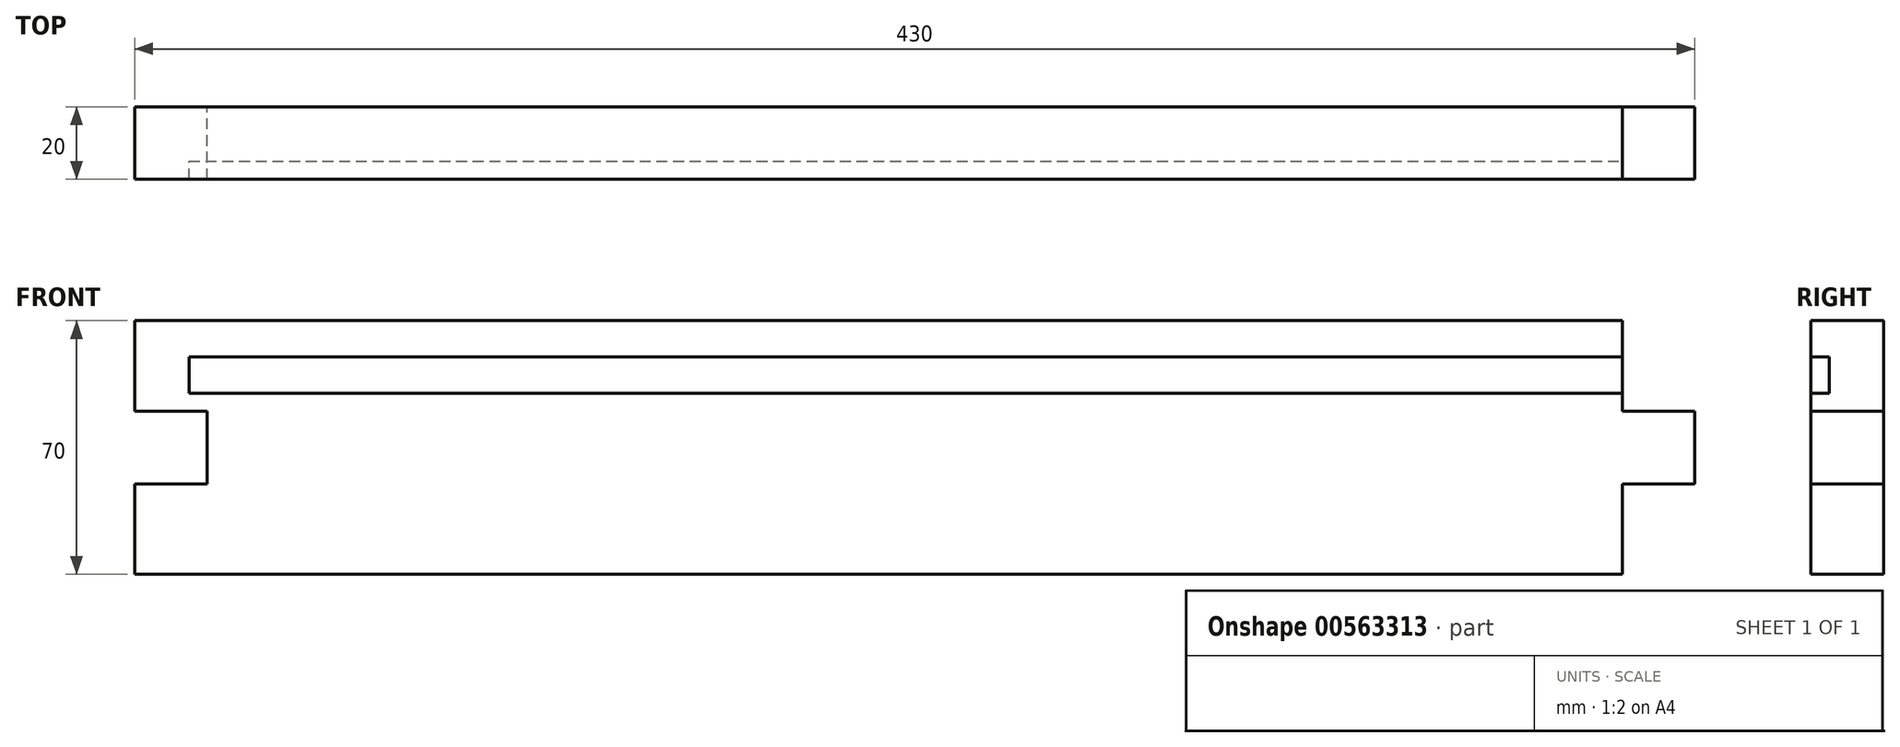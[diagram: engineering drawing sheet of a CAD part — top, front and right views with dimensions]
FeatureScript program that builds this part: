
annotation { "Feature Type Name" : "Feature", "Feature Type Description" : "" }
export const myFeature = defineFeature(function(context is Context, id is Id, definition is map)
    precondition{}
    {
        {
            var Q0;
            Q0=qCreatedBy(makeId("Top.planeOp"),FACE);
            var sketch = newSketch(context, id + "F0", { "sketchPlane" : qUnion([Q0])});
            skLineSegment(sketch, "E0.bottom", {"start": v(-404.74, -7.95) * mm, "end": v(25.26, -7.95) * mm});
            skLineSegment(sketch, "E0.top", {"start": v(-404.74, -27.95) * mm, "end": v(25.26, -27.95) * mm});
            skLineSegment(sketch, "E0.left", {"start": v(-404.74, -7.95) * mm, "end": v(-404.74, -27.95) * mm});
            skLineSegment(sketch, "E0.right", {"start": v(25.26, -7.95) * mm, "end": v(25.26, -27.95) * mm});
            skSolve(sketch);
        }
        {
            var Q0;
            Q0=qSketchRegion(id+"F0",true);
            extrude(context, id + "F1", {"entities" : qUnion([Q0]), "depth" : 70 * mm, "offsetDistance" : 25 * mm});
        }
        {
            var Q0;
            Q0=makeQuery(id+"F1.opExtrude","SWEPT_FACE",FACE,{"disambiguationData":[OSD([sQuery(id+"F0.wireOp",EDGE,"E0.right")])]});
            var sketch = newSketch(context, id + "F2", { "sketchPlane" : qUnion([Q0])});
            skLineSegment(sketch, "E1.bottom", {"start": v(-27.95, 60) * mm, "end": v(-22.95, 60) * mm});
            skLineSegment(sketch, "E1.top", {"start": v(-27.95, 50) * mm, "end": v(-22.95, 50) * mm});
            skLineSegment(sketch, "E1.left", {"start": v(-27.95, 60) * mm, "end": v(-27.95, 50) * mm});
            skLineSegment(sketch, "E1.right", {"start": v(-22.95, 60) * mm, "end": v(-22.95, 50) * mm});
            skSolve(sketch);
        }
        {
            var Q0;
            Q0=qSketchRegion(id+"F2",true);
            extrude(context, id + "F3", {"entities" : qUnion([Q0]), "operationType" : NewBodyOperationType.REMOVE, "oppositeDirection" : true, "depth" : 415 * mm, "offsetDistance" : 25 * mm, "hasSecondDirection" : true, "secondDirectionOppositeDirection" : true, "secondDirectionDepth" : 15 * mm});
        }
        {
            var Q0;
            Q0=makeQuery(id+"F1.opExtrude","SWEPT_FACE",FACE,{"disambiguationData":[OSD([sQuery(id+"F0.wireOp",EDGE,"E0.bottom")])]});
            var sketch = newSketch(context, id + "F4", { "sketchPlane" : qUnion([Q0])});
            skLineSegment(sketch, "E2.bottom", {"start": v(-25.26, 70) * mm, "end": v(-5.26, 70) * mm});
            skLineSegment(sketch, "E2.top", {"start": v(-25.26, 45) * mm, "end": v(-5.26, 45) * mm});
            skLineSegment(sketch, "E2.left", {"start": v(-25.26, 70) * mm, "end": v(-25.26, 45) * mm});
            skLineSegment(sketch, "E2.right", {"start": v(-5.26, 70) * mm, "end": v(-5.26, 45) * mm});
            skLineSegment(sketch, "E3.bottom", {"start": v(-25.26, 0) * mm, "end": v(-5.26, 0) * mm});
            skLineSegment(sketch, "E3.top", {"start": v(-25.26, 25) * mm, "end": v(-5.26, 25) * mm});
            skLineSegment(sketch, "E3.left", {"start": v(-25.26, 0) * mm, "end": v(-25.26, 25) * mm});
            skLineSegment(sketch, "E3.right", {"start": v(-5.26, 0) * mm, "end": v(-5.26, 25) * mm});
            skLineSegment(sketch, "E4.bottom", {"start": v(404.74, 45) * mm, "end": v(384.74, 45) * mm});
            skLineSegment(sketch, "E4.top", {"start": v(404.74, 25) * mm, "end": v(384.74, 25) * mm});
            skLineSegment(sketch, "E4.left", {"start": v(404.74, 45) * mm, "end": v(404.74, 25) * mm});
            skLineSegment(sketch, "E4.right", {"start": v(384.74, 45) * mm, "end": v(384.74, 25) * mm});
            skSolve(sketch);
        }
        {
            var Q0;
            Q0=makeQuery(id+"F4.imprint","IMPRINT",FACE,{"disambiguationData":[TD([[makeQuery(id+"F4.imprint","IMPRINT",EDGE,{"derivedFrom":sQuery(id+"F4.wireOp",EDGE,"E2.bottom")}),1.0]])]});
            var Q1;
            Q1=makeQuery(id+"F4.imprint","IMPRINT",FACE,{"disambiguationData":[TD([[makeQuery(id+"F4.imprint","IMPRINT",EDGE,{"derivedFrom":sQuery(id+"F4.wireOp",EDGE,"E3.bottom")}),-1.0]])]});
            var Q2;
            Q2=makeQuery(id+"F4.imprint","IMPRINT",FACE,{"disambiguationData":[TD([[makeQuery(id+"F4.imprint","IMPRINT",EDGE,{"derivedFrom":sQuery(id+"F4.wireOp",EDGE,"E4.bottom")}),1.0]])]});
            extrude(context, id + "F5", {"entities" : qUnion([Q0, Q1, Q2]), "operationType" : NewBodyOperationType.REMOVE, "endBound" : BoundingType.THROUGH_ALL, "oppositeDirection" : true, "depth" : 25 * mm, "offsetDistance" : 25 * mm});
        }
    });
